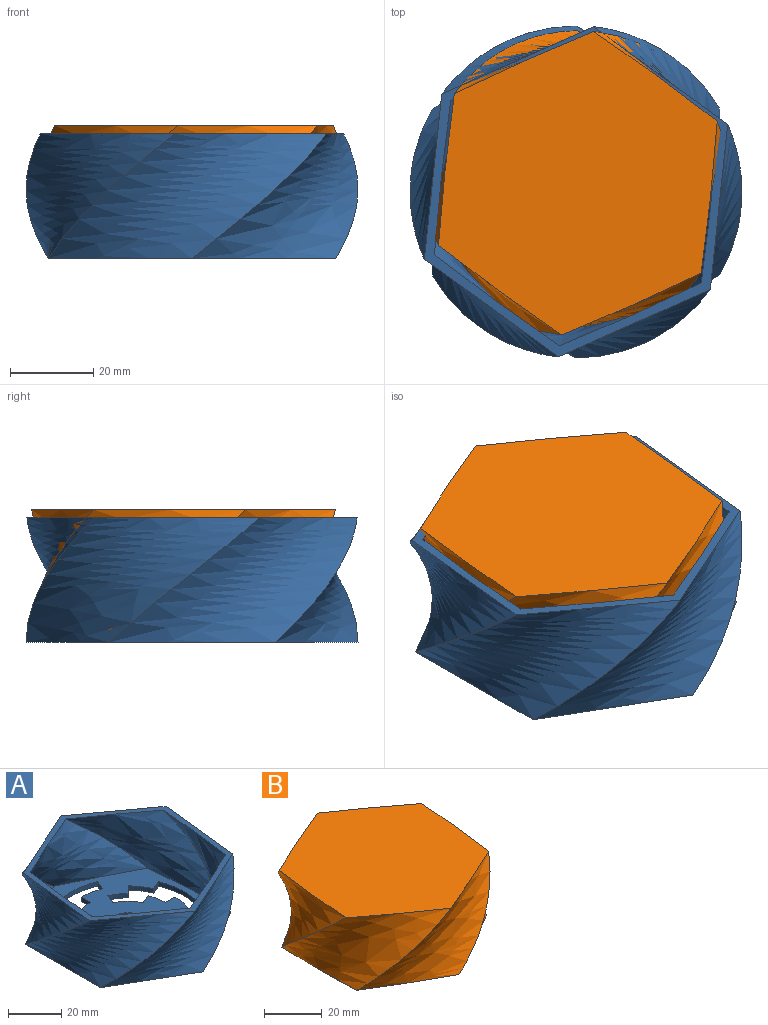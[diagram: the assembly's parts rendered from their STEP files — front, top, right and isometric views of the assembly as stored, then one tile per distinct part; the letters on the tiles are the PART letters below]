
ASSEMBLY  parts=2 mates=1
PART A: 58 faces, bbox 80.9x80.9x40 mm
  f0: plane 80x69.28mm, normal (0,0,-1), area 2919.9mm2, adj f3,f4,f5,f6,f7,f8,f9,f10
  f1: plane 74.53x66.9mm, normal (0,0,1), area 2430.2mm2, adj f9,f10,f11,f12,f13,f14,f15,f16
  f2: plane 79.56x73.08mm, normal (0,0,1), area 489.9mm2, adj f3,f4,f5,f6,f7,f8
  f3: bspline ~60.44x48.76mm, area 1274.8mm2, adj f0,f2,f4,f8
  f4: bspline ~72.68x40mm, area 1274.8mm2, adj f0,f2,f3,f5
  f5: bspline ~66.77x40.44mm, area 1274.8mm2, adj f0,f2,f4,f6
  f6: bspline ~60.44x48.76mm, area 1274.8mm2, adj f0,f2,f5,f7
  f7: bspline ~72.68x40mm, area 1274.8mm2, adj f0,f2,f6,f8
  f8: bspline ~66.77x40.44mm, area 1274.8mm2, adj f0,f2,f3,f7
  f9: cylinder r=7.5mm len=15mm, axis (0,0,-1), area 94.2mm2, adj f0,f1
  f10: cylinder r=20mm len=6.49mm, axis (0,0,-1), area 15.7mm2, adj f0,f1,f11,f21
  f11: plane 3.54x3.54mm, normal (0.71,0.71,0), area 10mm2, adj f0,f1,f10,f12
  f12: cylinder r=25mm len=8.11mm, axis (0,0,-1), area 19.6mm2, adj f0,f1,f11,f13
  f13: plane 4.62x2mm, normal (0.92,0.38,0), area 10mm2, adj f0,f1,f12,f14
  f14: cylinder r=30mm len=22.96mm, axis (0,0,-1), area 47.1mm2, adj f0,f1,f13,f15
  f15: plane 4.62x2mm, normal (-0.92,0.38,0), area 10mm2, adj f0,f1,f14,f16
  f16: cylinder r=25mm len=9.57mm, axis (0,0,-1), area 19.6mm2, adj f0,f1,f15,f17
  f17: plane 5x2mm, normal (-1,0,0), area 10mm2, adj f0,f1,f16,f18
  f18: cylinder r=20mm len=7.65mm, axis (0,0,-1), area 15.7mm2, adj f0,f1,f17,f19
  f19: plane 4.62x2mm, normal (-0.92,-0.38,0), area 10mm2, adj f0,f1,f18,f20
  f20: cylinder r=15mm len=8.12mm, axis (0,0,-1), area 23.6mm2, adj f0,f1,f19,f21
  f21: plane 4.62x2mm, normal (0.38,0.92,0), area 10mm2, adj f0,f1,f10,f20
  f22: cylinder r=15mm len=8.12mm, axis (0,0,-1), area 23.6mm2, adj f0,f1,f23,f33
  f23: plane 4.62x2mm, normal (-0.92,0.38,0), area 10mm2, adj f0,f1,f22,f24
  f24: cylinder r=20mm len=6.49mm, axis (0,0,-1), area 15.7mm2, adj f0,f1,f23,f25
  f25: plane 3.54x3.54mm, normal (-0.71,0.71,0), area 10mm2, adj f0,f1,f24,f26
  f26: cylinder r=25mm len=8.11mm, axis (0,0,-1), area 19.6mm2, adj f0,f1,f25,f27
  f27: plane 4.62x2mm, normal (-0.38,0.92,0), area 10mm2, adj f0,f1,f26,f28
  f28: cylinder r=30mm len=22.96mm, axis (0,0,-1), area 47.1mm2, adj f0,f1,f27,f29
  f29: plane 4.62x2mm, normal (-0.38,-0.92,0), area 10mm2, adj f0,f1,f28,f30
  f30: cylinder r=25mm len=9.57mm, axis (0,0,-1), area 19.6mm2, adj f0,f1,f29,f31
  f31: plane 5x2mm, normal (0,-1,0), area 10mm2, adj f0,f1,f30,f32
  f32: cylinder r=20mm len=7.65mm, axis (0,0,-1), area 15.7mm2, adj f0,f1,f31,f33
  f33: plane 4.62x2mm, normal (0.38,-0.92,0), area 10mm2, adj f0,f1,f22,f32
  f34: cylinder r=15mm len=8.12mm, axis (0,0,-1), area 23.6mm2, adj f0,f1,f35,f45
  f35: plane 4.62x2mm, normal (-0.38,-0.92,0), area 10mm2, adj f0,f1,f34,f36
  f36: cylinder r=20mm len=6.49mm, axis (0,0,-1), area 15.7mm2, adj f0,f1,f35,f37
  f37: plane 3.54x3.54mm, normal (-0.71,-0.71,0), area 10mm2, adj f0,f1,f36,f38
  f38: cylinder r=25mm len=8.11mm, axis (0,0,-1), area 19.6mm2, adj f0,f1,f37,f39
  f39: plane 4.62x2mm, normal (-0.92,-0.38,0), area 10mm2, adj f0,f1,f38,f40
  f40: cylinder r=30mm len=22.96mm, axis (0,0,-1), area 47.1mm2, adj f0,f1,f39,f41
  f41: plane 4.62x2mm, normal (0.92,-0.38,0), area 10mm2, adj f0,f1,f40,f42
  f42: cylinder r=25mm len=9.57mm, axis (0,0,-1), area 19.6mm2, adj f0,f1,f41,f43
  f43: plane 5x2mm, normal (1,0,0), area 10mm2, adj f0,f1,f42,f44
  f44: cylinder r=20mm len=7.65mm, axis (0,0,-1), area 15.7mm2, adj f0,f1,f43,f45
  f45: plane 4.62x2mm, normal (0.92,0.38,0), area 10mm2, adj f0,f1,f34,f44
  f46: cylinder r=20mm len=6.49mm, axis (0,0,-1), area 15.7mm2, adj f0,f1,f47,f57
  f47: plane 3.54x3.54mm, normal (0.71,-0.71,0), area 10mm2, adj f0,f1,f46,f48
  f48: cylinder r=25mm len=8.11mm, axis (0,0,-1), area 19.6mm2, adj f0,f1,f47,f49
  f49: plane 4.62x2mm, normal (0.38,-0.92,0), area 10mm2, adj f0,f1,f48,f50
  f50: cylinder r=30mm len=22.96mm, axis (0,0,-1), area 47.1mm2, adj f0,f1,f49,f51
  f51: plane 4.62x2mm, normal (0.38,0.92,0), area 10mm2, adj f0,f1,f50,f52
  f52: cylinder r=25mm len=9.57mm, axis (0,0,-1), area 19.6mm2, adj f0,f1,f51,f53
  f53: plane 5x2mm, normal (0,1,0), area 10mm2, adj f0,f1,f52,f54
  f54: cylinder r=20mm len=7.65mm, axis (0,0,-1), area 15.7mm2, adj f0,f1,f53,f55
  f55: plane 4.62x2mm, normal (-0.38,0.92,0), area 10mm2, adj f0,f1,f54,f56
  f56: cylinder r=15mm len=8.12mm, axis (0,0,-1), area 23.6mm2, adj f0,f1,f55,f57
  f57: plane 4.62x2mm, normal (0.92,-0.38,0), area 10mm2, adj f0,f1,f46,f56
PART B: 9 faces, bbox 74.4x73.5x40 mm
  f0: plane 73.54x64.29mm, normal (0,0,-1), area 444.4mm2, adj f1,f3,f4,f5,f6,f7
  f1: bspline ~63.89x40mm, area 1155.6mm2, adj f0,f2,f3,f7
  f2: plane 73.14x67.18mm, normal (0,0,1), area 3555.7mm2, adj f1,f3,f4,f5,f6,f7
  f3: bspline ~65.71x40mm, area 1155.6mm2, adj f0,f1,f2,f4
  f4: bspline ~51.73x48.54mm, area 1155.6mm2, adj f0,f2,f3,f5
  f5: bspline ~63.89x40mm, area 1155.6mm2, adj f0,f2,f4,f6
  f6: bspline ~65.71x40mm, area 1155.6mm2, adj f0,f2,f5,f7
  f7: bspline ~51.73x48.54mm, area 1155.6mm2, adj f0,f1,f2,f6
  f8: plane 67.5x64.17mm, normal (0,0,-1), area 3111.5mm2
PLACE A t=(38.99,-19.74,8.75)mm
PLACE B t=(39.43,-17.69,10.75)mm
MATE planar A.f1 <-> B.f0  axis (0,0,1) through (13.59,-9.22,10.75)mm
